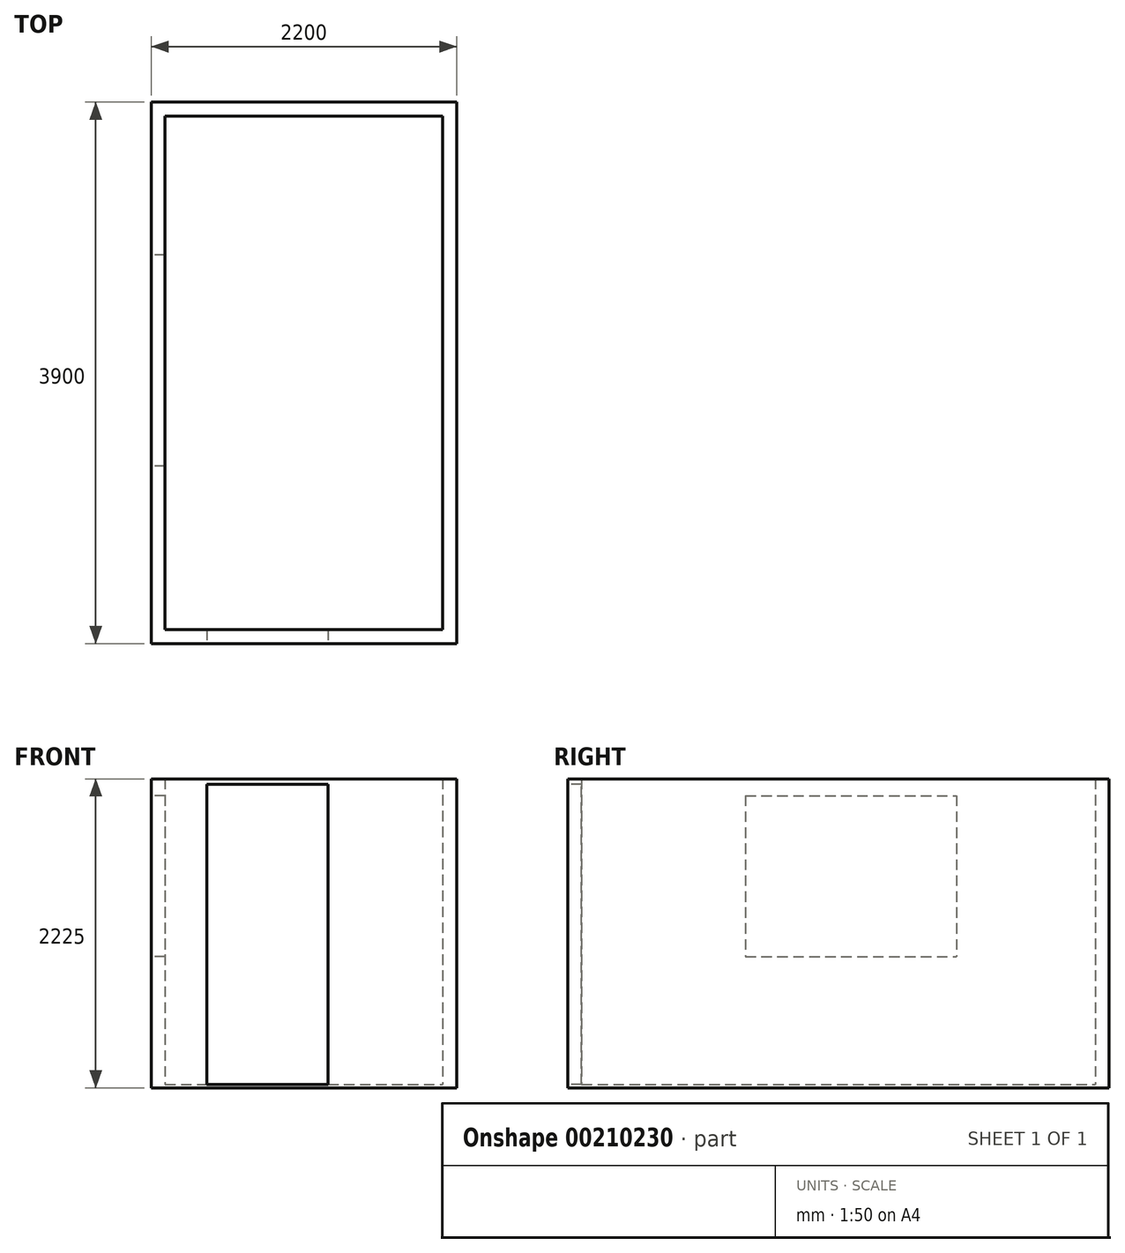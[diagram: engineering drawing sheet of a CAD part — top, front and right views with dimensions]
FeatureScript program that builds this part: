
annotation { "Feature Type Name" : "Feature", "Feature Type Description" : "" }
export const myFeature = defineFeature(function(context is Context, id is Id, definition is map)
    precondition{}
    {
        {
            var Q0;
            Q0=qCreatedBy(makeId("Top.planeOp"),FACE);
            var sketch = newSketch(context, id + "F0", { "sketchPlane" : qUnion([Q0])});
            skLineSegment(sketch, "E0.bottom", {"start": v(0, 0) * mm, "end": v(2000, 0) * mm});
            skLineSegment(sketch, "E0.top", {"start": v(0, 3700) * mm, "end": v(2000, 3700) * mm});
            skLineSegment(sketch, "E0.left", {"start": v(0, 0) * mm, "end": v(0, 3700) * mm});
            skLineSegment(sketch, "E0.right", {"start": v(2000, 0) * mm, "end": v(2000, 3700) * mm});
            skLineSegment(sketch, "E1.0", {"start": v(2100, -100) * mm, "end": v(2100, 3800) * mm});
            skLineSegment(sketch, "E1.1", {"start": v(-100, -100) * mm, "end": v(2100, -100) * mm});
            skLineSegment(sketch, "E1.2", {"start": v(-100, -100) * mm, "end": v(-100, 3800) * mm});
            skLineSegment(sketch, "E1.3", {"start": v(-100, 3800) * mm, "end": v(2100, 3800) * mm});
            skSolve(sketch);
        }
        {
            var Q0;
            Q0=makeQuery(id+"F0.imprint","IMPRINT",FACE,{"disambiguationData":[TD([[makeQuery(id+"F0.imprint","IMPRINT",EDGE,{"derivedFrom":sQuery(id+"F0.wireOp",EDGE,"E0.bottom")}),-1.0]])]});
            extrude(context, id + "F1", {"entities" : qUnion([Q0]), "depth" : 2200 * mm, "offsetDistance" : 25 * mm});
        }
        {
            var Q0;
            Q0=makeQuery(id+"F0.imprint","IMPRINT",FACE,{"disambiguationData":[TD([[makeQuery(id+"F0.imprint","IMPRINT",EDGE,{"derivedFrom":sQuery(id+"F0.wireOp",EDGE,"E0.bottom")}),1.0]])]});
            var Q1;
            Q1=makeQuery(id+"F0.imprint","IMPRINT",FACE,{"disambiguationData":[TD([[makeQuery(id+"F0.imprint","IMPRINT",EDGE,{"derivedFrom":sQuery(id+"F0.wireOp",EDGE,"E0.bottom")}),-1.0]])]});
            extrude(context, id + "F2", {"entities" : qUnion([Q0, Q1]), "operationType" : NewBodyOperationType.ADD, "oppositeDirection" : true, "depth" : 25 * mm, "offsetDistance" : 25 * mm});
        }
        {
            var Q0;
            {var subQ0=sQuery(id+"F0.wireOp",EDGE,"E1.1");Q0=makeQuery(id+"F2.boolean.opBoolean","MERGE",FACE,{"derivedFrom":[makeQuery(id+"F1.opExtrude","SWEPT_FACE",FACE,{"disambiguationData":[OSD([subQ0])]}),makeQuery(id+"F2.opExtrude","SWEPT_FACE",FACE,{"disambiguationData":[OSD([subQ0])]})]});}
            var sketch = newSketch(context, id + "F3", { "sketchPlane" : qUnion([Q0])});
            skLineSegment(sketch, "E2.bottom", {"start": v(300, 0) * mm, "end": v(1174.1, 0) * mm});
            skLineSegment(sketch, "E2.top", {"start": v(300, 2160) * mm, "end": v(1174.1, 2160) * mm});
            skLineSegment(sketch, "E2.left", {"start": v(300, 0) * mm, "end": v(300, 2160) * mm});
            skLineSegment(sketch, "E2.right", {"start": v(1174.1, 0) * mm, "end": v(1174.1, 2160) * mm});
            skLineSegment(sketch, "E3.0.1", {"start": v(0, 0) * mm, "end": v(2000, 0) * mm, "construction": true});
            skLineSegment(sketch, "E3.0.3", {"start": v(2000, 0) * mm, "end": v(0, 0) * mm});
            skSolve(sketch);
        }
        {
            var Q0;
            Q0=makeQuery(id+"F3.imprint","IMPRINT",FACE,{"disambiguationData":[TD([[makeQuery(id+"F3.imprint","IMPRINT",EDGE,{"derivedFrom":sQuery(id+"F3.wireOp",EDGE,"E2.top")}),-1.0]])]});
            extrude(context, id + "F4", {"entities" : qUnion([Q0]), "operationType" : NewBodyOperationType.REMOVE, "endBound" : BoundingType.UP_TO_NEXT, "oppositeDirection" : true, "depth" : 961.15 * mm, "offsetDistance" : 25 * mm});
        }
        {
            var Q0;
            {var subQ0=sQuery(id+"F0.wireOp",EDGE,"E1.2");Q0=makeQuery(id+"F2.boolean.opBoolean","MERGE",FACE,{"derivedFrom":[makeQuery(id+"F1.opExtrude","SWEPT_FACE",FACE,{"disambiguationData":[OSD([subQ0])]}),makeQuery(id+"F2.opExtrude","SWEPT_FACE",FACE,{"disambiguationData":[OSD([subQ0])]})]});}
            var sketch = newSketch(context, id + "F5", { "sketchPlane" : qUnion([Q0])});
            skLineSegment(sketch, "E4.bottom", {"start": v(-2700, 920) * mm, "end": v(-1180, 920) * mm});
            skLineSegment(sketch, "E4.top", {"start": v(-2700, 2080) * mm, "end": v(-1180, 2080) * mm});
            skLineSegment(sketch, "E4.left", {"start": v(-2700, 920) * mm, "end": v(-2700, 2080) * mm});
            skLineSegment(sketch, "E4.right", {"start": v(-1180, 920) * mm, "end": v(-1180, 2080) * mm});
            skSolve(sketch);
        }
        {
            var Q0;
            Q0=makeQuery(id+"F5.imprint","IMPRINT",FACE,{"disambiguationData":[TD([[makeQuery(id+"F5.imprint","IMPRINT",EDGE,{"derivedFrom":sQuery(id+"F5.wireOp",EDGE,"E4.bottom")}),1.0]])]});
            extrude(context, id + "F6", {"entities" : qUnion([Q0]), "operationType" : NewBodyOperationType.REMOVE, "endBound" : BoundingType.UP_TO_NEXT, "oppositeDirection" : true, "depth" : 25 * mm, "offsetDistance" : 25 * mm});
        }
    });
